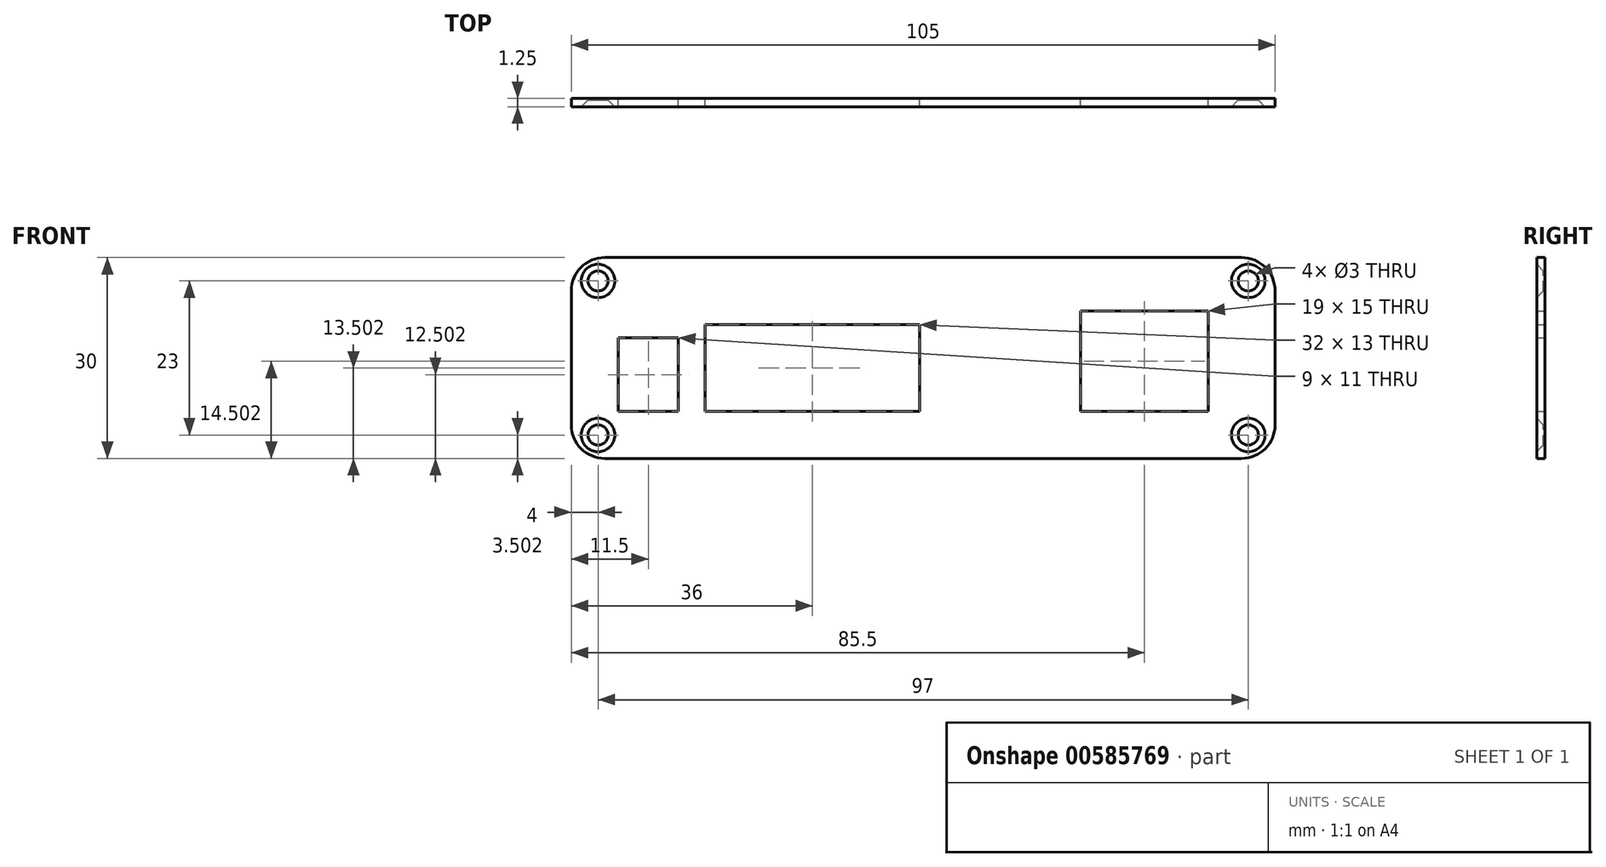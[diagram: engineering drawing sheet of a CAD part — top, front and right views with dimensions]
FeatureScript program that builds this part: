
annotation { "Feature Type Name" : "Feature", "Feature Type Description" : "" }
export const myFeature = defineFeature(function(context is Context, id is Id, definition is map)
    precondition{}
    {
        {
            var Q0;
            Q0=qCreatedBy(makeId("Front.planeOp"),FACE);
            var sketch = newSketch(context, id + "F0", { "sketchPlane" : qUnion([Q0])});
            skLineSegment(sketch, "E0.bottom", {"start": v(-52, 10.3) * mm, "end": v(53, 10.3) * mm});
            skLineSegment(sketch, "E0.top", {"start": v(-52, -19.7) * mm, "end": v(53, -19.7) * mm});
            skLineSegment(sketch, "E0.left", {"start": v(-52, 10.3) * mm, "end": v(-52, -19.7) * mm});
            skLineSegment(sketch, "E0.right", {"start": v(53, 10.3) * mm, "end": v(53, -19.7) * mm});
            skCircle(sketch, "E1", {"center": v(49, 6.8) * mm, "radius": 1.5 * mm});
            skCircle(sketch, "E2", {"center": v(49, -16.2) * mm, "radius": 1.5 * mm});
            skCircle(sketch, "E3", {"center": v(-48, 6.8) * mm, "radius": 1.5 * mm});
            skCircle(sketch, "E4", {"center": v(-48, -16.2) * mm, "radius": 1.5 * mm});
            skLineSegment(sketch, "E5.bottom", {"start": v(-45, -1.7) * mm, "end": v(-36, -1.7) * mm});
            skLineSegment(sketch, "E5.top", {"start": v(-45, -12.7) * mm, "end": v(-36, -12.7) * mm});
            skLineSegment(sketch, "E5.left", {"start": v(-45, -1.7) * mm, "end": v(-45, -12.7) * mm});
            skLineSegment(sketch, "E5.right", {"start": v(-36, -1.7) * mm, "end": v(-36, -12.7) * mm});
            skLineSegment(sketch, "E6.bottom", {"start": v(-32, 0.3) * mm, "end": v(0, 0.3) * mm});
            skLineSegment(sketch, "E6.top", {"start": v(-32, -12.7) * mm, "end": v(0, -12.7) * mm});
            skLineSegment(sketch, "E6.left", {"start": v(-32, 0.3) * mm, "end": v(-32, -12.7) * mm});
            skLineSegment(sketch, "E6.right", {"start": v(0, 0.3) * mm, "end": v(0, -12.7) * mm});
            skLineSegment(sketch, "E7.bottom", {"start": v(24, 2.3) * mm, "end": v(43, 2.3) * mm});
            skLineSegment(sketch, "E7.top", {"start": v(24, -12.7) * mm, "end": v(43, -12.7) * mm});
            skLineSegment(sketch, "E7.left", {"start": v(24, 2.3) * mm, "end": v(24, -12.7) * mm});
            skLineSegment(sketch, "E7.right", {"start": v(43, 2.3) * mm, "end": v(43, -12.7) * mm});
            skSolve(sketch);
        }
        {
            var Q0;
            Q0=makeQuery(id+"F0.imprint","IMPRINT",FACE,{"disambiguationData":[TD([[makeQuery(id+"F0.imprint","IMPRINT",EDGE,{"derivedFrom":sQuery(id+"F0.wireOp",EDGE,"E0.bottom")}),-1.0]])]});
            extrude(context, id + "F1", {"entities" : qUnion([Q0]), "depth" : 1.25 * mm, "offsetDistance" : 25 * mm});
        }
        {
            var Q0;
            Q0=makeQuery(id+"F1.opExtrude","SWEPT_EDGE",EDGE,{"disambiguationData":[OSD([sQuery(id+"F0.wireOp",EDGE,"E0.bottom"),sQuery(id+"F0.wireOp",EDGE,"E0.right")])]});
            var Q1;
            Q1=makeQuery(id+"F1.opExtrude","SWEPT_EDGE",EDGE,{"disambiguationData":[OSD([sQuery(id+"F0.wireOp",EDGE,"E0.top"),sQuery(id+"F0.wireOp",EDGE,"E0.right")])]});
            var Q2;
            Q2=makeQuery(id+"F1.opExtrude","SWEPT_EDGE",EDGE,{"disambiguationData":[OSD([sQuery(id+"F0.wireOp",EDGE,"E0.top"),sQuery(id+"F0.wireOp",EDGE,"E0.left")])]});
            var Q3;
            Q3=makeQuery(id+"F1.opExtrude","SWEPT_EDGE",EDGE,{"disambiguationData":[OSD([sQuery(id+"F0.wireOp",EDGE,"E0.bottom"),sQuery(id+"F0.wireOp",EDGE,"E0.left")])]});
            fillet(context, id + "F2", {"entities" : qUnion([Q0, Q1, Q2, Q3]), "radius" : 5 * mm, "tangentPropagation" : true, "allowEdgeOverflow" : false});
        }
        {
            var Q0;
            Q0=makeQuery(id+"F1.opExtrude","CAP_EDGE",EDGE,{"disambiguationData":[OSD([sQuery(id+"F0.wireOp",EDGE,"E1")])],"isStart":false});
            var Q1;
            Q1=makeQuery(id+"F1.opExtrude","CAP_EDGE",EDGE,{"disambiguationData":[OSD([sQuery(id+"F0.wireOp",EDGE,"E2")])],"isStart":false});
            var Q2;
            Q2=makeQuery(id+"F1.opExtrude","CAP_EDGE",EDGE,{"disambiguationData":[OSD([sQuery(id+"F0.wireOp",EDGE,"E4")])],"isStart":false});
            var Q3;
            Q3=makeQuery(id+"F1.opExtrude","CAP_EDGE",EDGE,{"disambiguationData":[OSD([sQuery(id+"F0.wireOp",EDGE,"E3")])],"isStart":false});
            chamfer(context, id + "F3", {"entities" : qUnion([Q0, Q1, Q2, Q3]), "width" : 1 * mm, "tangentPropagation" : true});
        }
    });
